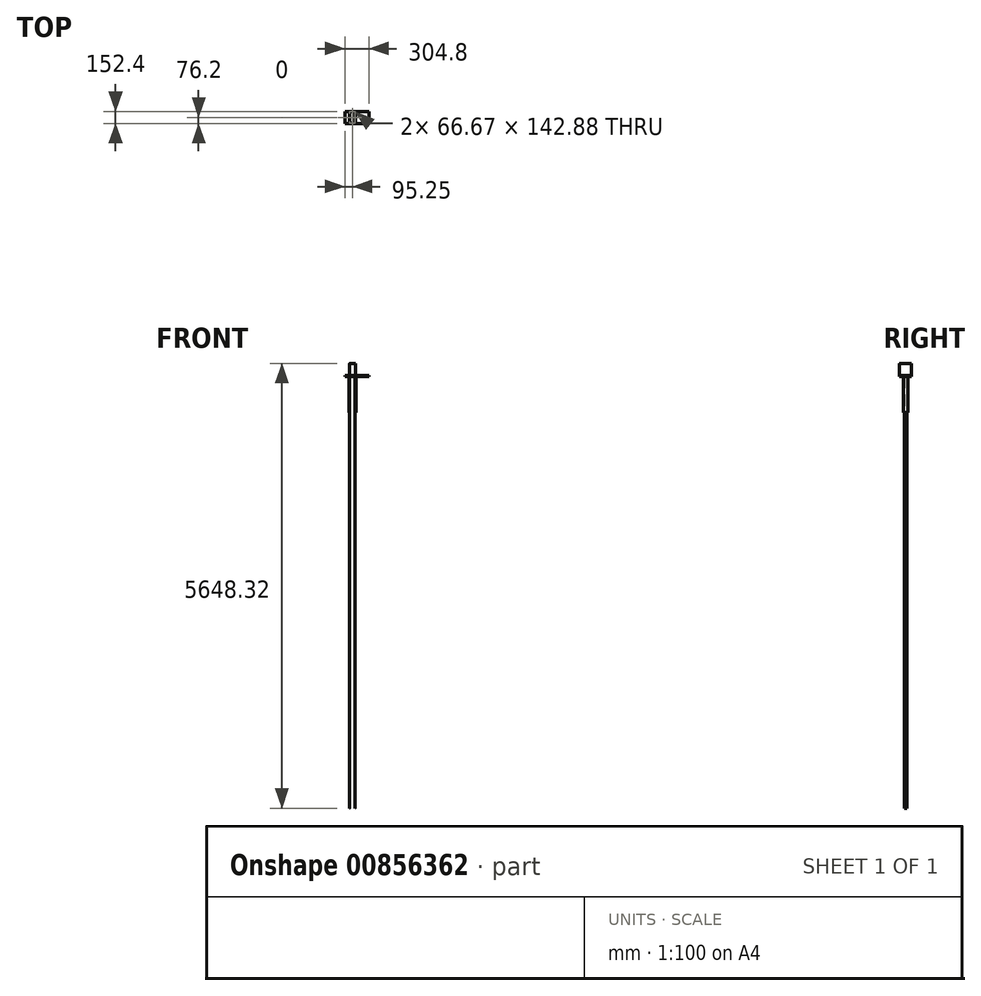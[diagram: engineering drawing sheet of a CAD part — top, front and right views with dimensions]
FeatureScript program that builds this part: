
annotation { "Feature Type Name" : "Feature", "Feature Type Description" : "" }
export const myFeature = defineFeature(function(context is Context, id is Id, definition is map)
    precondition{}
    {
        {
            var Q0;
            Q0=qCreatedBy(makeId("Top.planeOp"),FACE);
            var sketch = newSketch(context, id + "F0", { "sketchPlane" : qUnion([Q0])});
            skCircle(sketch, "E0", {"center": v(0, 0) * mm, "radius": 36.51 * mm});
            skCircle(sketch, "E1", {"center": v(0, 0) * mm, "radius": 31.75 * mm});
            skSolve(sketch);
        }
        {
            var Q0;
            Q0 = qSketchRegion(id + "F0", true);
            extrude(context, id + "F1", {"entities" : qUnion([Q0]), "depth" : 5486.4 * mm, "offsetDistance" : 25.4 * mm});
        }
        {
            var Q0;
            Q0=makeQuery(id+"F1.opExtrude","CAP_FACE",FACE,{"disambiguationData":[OSD([sQuery(id+"F0.wireOp",EDGE,"E0"),sQuery(id+"F0.wireOp",EDGE,"E1")])],"isStart":false});
            var sketch = newSketch(context, id + "F2", { "sketchPlane" : qUnion([Q0])});
            skCircle(sketch, "E2", {"center": v(0, 0) * mm, "radius": 38.96 * mm});
            skCircle(sketch, "E3", {"center": v(0, 0) * mm, "radius": 44.45 * mm});
            skSolve(sketch);
        }
        {
            var Q0;
            Q0 = qSketchRegion(id + "F2", true);
            extrude(context, id + "F3", {"entities" : qUnion([Q0]), "oppositeDirection" : true, "depth" : 457.2 * mm, "offsetDistance" : 25.4 * mm});
        }
        {
            var Q0;
            Q0=makeQuery(id+"F3.opExtrude","CAP_FACE",FACE,{"disambiguationData":[OSD([sQuery(id+"F2.wireOp",EDGE,"E2"),sQuery(id+"F2.wireOp",EDGE,"E3")])],"isStart":true});
            var sketch = newSketch(context, id + "F4", { "sketchPlane" : qUnion([Q0])});
            skLineSegment(sketch, "E4.bottom", {"start": v(-95.25, 76.2) * mm, "end": v(209.55, 76.2) * mm});
            skLineSegment(sketch, "E4.top", {"start": v(-95.25, -76.2) * mm, "end": v(209.55, -76.2) * mm});
            skLineSegment(sketch, "E4.left", {"start": v(-95.25, 76.2) * mm, "end": v(-95.25, -76.2) * mm});
            skLineSegment(sketch, "E4.right", {"start": v(209.55, 76.2) * mm, "end": v(209.55, -76.2) * mm});
            skSolve(sketch);
        }
        {
            var Q0;
            Q0 = qSketchRegion(id + "F4", true);
            extrude(context, id + "F5", {"entities" : qUnion([Q0]), "depth" : 9.52 * mm, "offsetDistance" : 25.4 * mm});
        }
        {
            var Q0;
            Q0=makeQuery(id+"F5.opExtrude","CAP_FACE",FACE,{"disambiguationData":[OSD([sQuery(id+"F4.wireOp",EDGE,"E4.bottom"),sQuery(id+"F4.wireOp",EDGE,"E4.top"),sQuery(id+"F4.wireOp",EDGE,"E4.left"),sQuery(id+"F4.wireOp",EDGE,"E4.right")])],"isStart":false});
            var sketch = newSketch(context, id + "F6", { "sketchPlane" : qUnion([Q0])});
            skLineSegment(sketch, "E5.bottom", {"start": v(-38.1, 76.2) * mm, "end": v(38.1, 76.2) * mm});
            skLineSegment(sketch, "E5.top", {"start": v(-38.1, -76.2) * mm, "end": v(38.1, -76.2) * mm});
            skLineSegment(sketch, "E5.left", {"start": v(-38.1, 76.2) * mm, "end": v(-38.1, -76.2) * mm});
            skLineSegment(sketch, "E5.right", {"start": v(38.1, 76.2) * mm, "end": v(38.1, -76.2) * mm});
            skSolve(sketch);
        }
        {
            var Q0;
            Q0 = qSketchRegion(id + "F6", true);
            extrude(context, id + "F7", {"entities" : qUnion([Q0]), "depth" : 152.4 * mm, "offsetDistance" : 25.4 * mm});
        }
        {
            var Q0;
            Q0=makeQuery(id+"F7.opExtrude","SWEPT_EDGE",EDGE,{"disambiguationData":[OSD([sQuery(id+"F4.wireOp",EDGE,"E4.top"),sQuery(id+"F6.wireOp",EDGE,"E5.top"),sQuery(id+"F6.wireOp",EDGE,"E5.left")])]});
            var Q1;
            Q1=makeQuery(id+"F7.opExtrude","SWEPT_EDGE",EDGE,{"disambiguationData":[OSD([sQuery(id+"F4.wireOp",EDGE,"E4.top"),sQuery(id+"F6.wireOp",EDGE,"E5.top"),sQuery(id+"F6.wireOp",EDGE,"E5.right")])]});
            var Q2;
            Q2=makeQuery(id+"F7.opExtrude","SWEPT_EDGE",EDGE,{"disambiguationData":[OSD([sQuery(id+"F4.wireOp",EDGE,"E4.bottom"),sQuery(id+"F6.wireOp",EDGE,"E5.bottom"),sQuery(id+"F6.wireOp",EDGE,"E5.left")])]});
            var Q3;
            Q3=makeQuery(id+"F7.opExtrude","SWEPT_EDGE",EDGE,{"disambiguationData":[OSD([sQuery(id+"F4.wireOp",EDGE,"E4.bottom"),sQuery(id+"F6.wireOp",EDGE,"E5.bottom"),sQuery(id+"F6.wireOp",EDGE,"E5.right")])]});
            fillet(context, id + "F8", {"entities" : qUnion([Q0, Q1, Q2, Q3]), "radius" : 4.76 * mm, "tangentPropagation" : true, "allowEdgeOverflow" : false});
        }
        {
            var Q0;
            Q0=makeQuery(id+"F7.opExtrude","CAP_FACE",FACE,{"disambiguationData":[OSD([sQuery(id+"F6.wireOp",EDGE,"E5.bottom"),sQuery(id+"F6.wireOp",EDGE,"E5.top"),sQuery(id+"F6.wireOp",EDGE,"E5.left"),sQuery(id+"F6.wireOp",EDGE,"E5.right")])],"isStart":false});
            var sketch = newSketch(context, id + "F9", { "sketchPlane" : qUnion([Q0])});
            skLineSegment(sketch, "E6.0", {"start": v(33.34, -71.44) * mm, "end": v(33.34, 71.44) * mm});
            skLineSegment(sketch, "E6.1", {"start": v(-33.34, -71.44) * mm, "end": v(33.34, -71.44) * mm});
            skLineSegment(sketch, "E6.2", {"start": v(-33.34, 71.44) * mm, "end": v(-33.34, -71.44) * mm});
            skLineSegment(sketch, "E6.3", {"start": v(33.34, 71.44) * mm, "end": v(-33.34, 71.44) * mm});
            skSolve(sketch);
        }
        {
            var Q0;
            Q0 = qSketchRegion(id + "F9", true);
            extrude(context, id + "F10", {"entities" : qUnion([Q0]), "operationType" : NewBodyOperationType.REMOVE, "endBound" : BoundingType.THROUGH_ALL, "oppositeDirection" : true, "depth" : 25.4 * mm, "offsetDistance" : 25.4 * mm});
        }
    });
